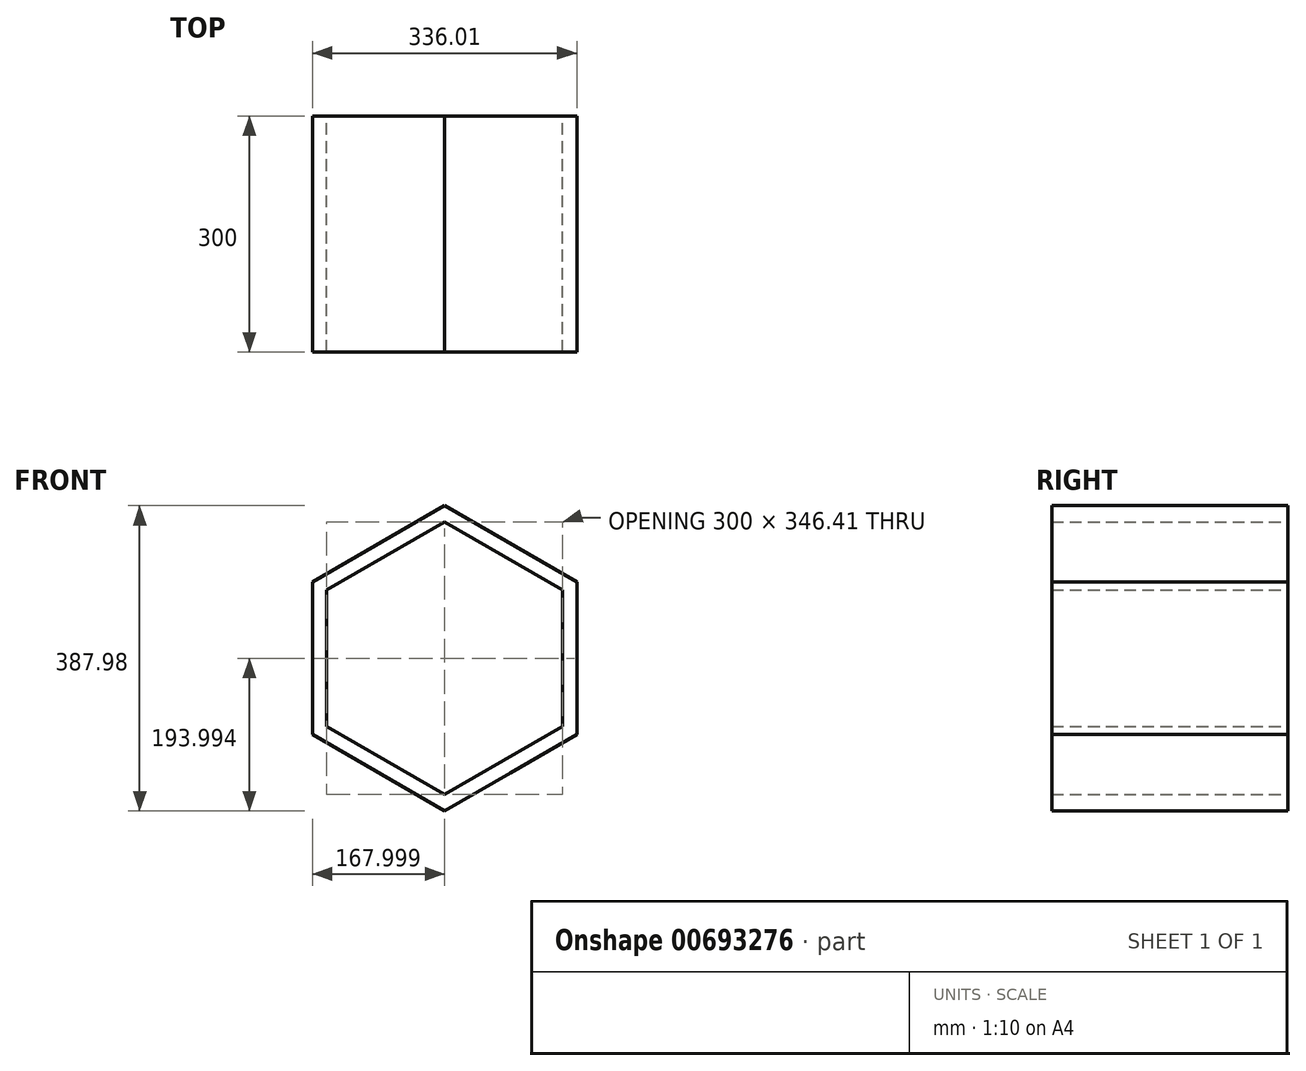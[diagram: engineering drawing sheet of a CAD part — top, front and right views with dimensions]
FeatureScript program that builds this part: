
annotation { "Feature Type Name" : "Feature", "Feature Type Description" : "" }
export const myFeature = defineFeature(function(context is Context, id is Id, definition is map)
    precondition{}
    {
        {
            var Q0;
            Q0=qCreatedBy(makeId("Front.planeOp"),FACE);
            var sketch = newSketch(context, id + "F0", { "sketchPlane" : qUnion([Q0])});
            skCircle(sketch, "E0.cCircle", {"center": v(0, 0) * mm, "radius": 150 * mm, "construction": true});
            skLineSegment(sketch, "E0.0", {"start": v(-150, 86.6) * mm, "end": v(0, 173.2) * mm});
            skLineSegment(sketch, "E0.1", {"start": v(0, 173.2) * mm, "end": v(150, 86.6) * mm});
            skLineSegment(sketch, "E0.2", {"start": v(150, 86.6) * mm, "end": v(150, -86.6) * mm});
            skLineSegment(sketch, "E0.3", {"start": v(150, -86.6) * mm, "end": v(0, -173.2) * mm});
            skLineSegment(sketch, "E0.4", {"start": v(0, -173.2) * mm, "end": v(-150, -86.6) * mm});
            skLineSegment(sketch, "E0.5", {"start": v(-150, -86.6) * mm, "end": v(-150, 86.6) * mm});
            skPoint(sketch, "E0.0.midPoint", {"position": v(-75, 129.9) * mm});
            skSolve(sketch);
        }
        {
            var Q0;
            Q0=qCreatedBy(makeId("Front.planeOp"),FACE);
            var sketch = newSketch(context, id + "F1", { "sketchPlane" : qUnion([Q0])});
            skLineSegment(sketch, "E1", {"start": v(-190.32, 109.87) * mm, "end": v(214.44, -123.8) * mm, "construction": true});
            skLineSegment(sketch, "E2", {"start": v(207.34, 119.71) * mm, "end": v(-214.42, -123.8) * mm, "construction": true});
            skLineSegment(sketch, "E3", {"start": v(0, 206.1) * mm, "end": v(0, -210.89) * mm, "construction": true});
            skSolve(sketch);
        }
        {
            var Q0;
            Q0=qCreatedBy(makeId("Front.planeOp"),FACE);
            cPlane(context, id + "F2", {"entities" : qUnion([Q0]), "cplaneType" : CPlaneType.OFFSET, "offset" : 25 * mm, "width" : 150 * mm, "height" : 150 * mm});
        }
        {
            var Q0;
            Q0=qCreatedBy(id+"F2.planeOp",FACE);
            var sketch = newSketch(context, id + "F3", { "sketchPlane" : qUnion([Q0])});
            skLineSegment(sketch, "E4", {"start": v(-150, 86.6) * mm, "end": v(0, 173.2) * mm});
            skLineSegment(sketch, "E5", {"start": v(0, 173.2) * mm, "end": v(0, 194) * mm});
            skLineSegment(sketch, "E6", {"start": v(0, 194) * mm, "end": v(-168, 97) * mm});
            skLineSegment(sketch, "E7", {"start": v(-168, 97) * mm, "end": v(-150, 86.6) * mm});
            skSolve(sketch);
        }
        {
            var Q0;
            Q0=makeQuery(id+"F3.imprint","IMPRINT",FACE,{"disambiguationData":[TD([[makeQuery(id+"F3.imprint","IMPRINT",EDGE,{"derivedFrom":sQuery(id+"F3.wireOp",EDGE,"E4")}),1.0]])]});
            extrude(context, id + "F4", {"entities" : qUnion([Q0]), "depth" : 300 * mm, "offsetDistance" : 25 * mm});
        }
        {
            var Q0;
            Q0=makeQuery(id+"F4.opExtrude","SWEPT_BODY",BODY,{"disambiguationData":[OSD([sQuery(id+"F3.wireOp",EDGE,"E4"),sQuery(id+"F3.wireOp",EDGE,"E5"),sQuery(id+"F3.wireOp",EDGE,"E6"),sQuery(id+"F3.wireOp",EDGE,"E7")])]});
            var Q1;
            Q1=makeQuery(id+"F4.opExtrude","SWEPT_FACE",FACE,{"disambiguationData":[OSD([sQuery(id+"F3.wireOp",EDGE,"E5")])]});
            mirror(context, id + "F5", {"operationType" : NewBodyOperationType.ADD, "entities" : qUnion([Q0]), "mirrorPlane" : qUnion([Q1])});
        }
        {
            var Q0;
            Q0=makeQuery(id+"F4.opExtrude","SWEPT_BODY",BODY,{"disambiguationData":[OSD([sQuery(id+"F3.wireOp",EDGE,"E4"),sQuery(id+"F3.wireOp",EDGE,"E5"),sQuery(id+"F3.wireOp",EDGE,"E6"),sQuery(id+"F3.wireOp",EDGE,"E7")])]});
            var Q1;
            Q1=makeQuery(id+"F5.opPattern","COPY",FACE,{"derivedFrom":makeQuery(id+"F4.opExtrude","SWEPT_FACE",FACE,{"disambiguationData":[OSD([sQuery(id+"F3.wireOp",EDGE,"E7")])]}),"instanceName":"1"});
            mirror(context, id + "F6", {"operationType" : NewBodyOperationType.ADD, "entities" : qUnion([Q0]), "mirrorPlane" : qUnion([Q1])});
        }
        {
            var Q0;
            Q0=makeQuery(id+"F4.opExtrude","SWEPT_BODY",BODY,{"disambiguationData":[OSD([sQuery(id+"F3.wireOp",EDGE,"E4"),sQuery(id+"F3.wireOp",EDGE,"E5"),sQuery(id+"F3.wireOp",EDGE,"E6"),sQuery(id+"F3.wireOp",EDGE,"E7")])]});
            var Q1;
            Q1=makeQuery(id+"F4.opExtrude","SWEPT_FACE",FACE,{"disambiguationData":[OSD([sQuery(id+"F3.wireOp",EDGE,"E7")])]});
            mirror(context, id + "F7", {"operationType" : NewBodyOperationType.ADD, "entities" : qUnion([Q0]), "mirrorPlane" : qUnion([Q1])});
        }
    });
